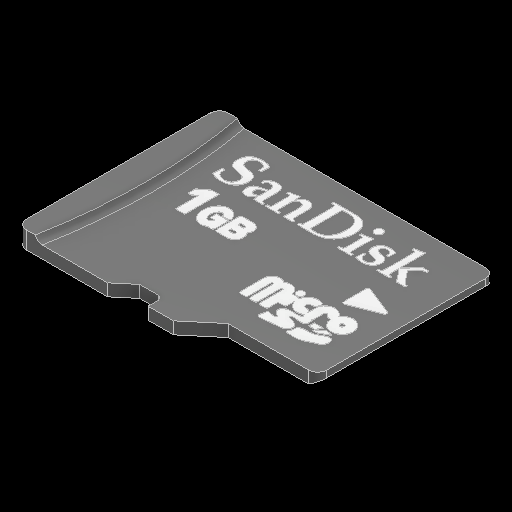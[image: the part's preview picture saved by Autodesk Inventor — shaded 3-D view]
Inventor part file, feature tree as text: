
AUTODESK INVENTOR PART (.ipt)
format: ipt  version: 2023 (Build 270158000, 158)  size: 673,280 bytes
history: native  units: in
note: dims shown in document units (in); Inventor stores cm internally (conversion verified against a paired STEP export)
features: chamfer x1
ambient origin geometry x8: Origin, YZ Plane, XZ Plane, XY Plane, X Axis, Y Axis, Z Axis, Center Point
bodies: Solid1 (feature_tree)
feature tree (1):
  chamfer  "Chamfer1"  [1 undecoded]
note: 1 required parameter value undecoded (feature->parameter linkage not recoverable at this tier; creation-order binding heuristic only, values carry confidence <= 0.55)
